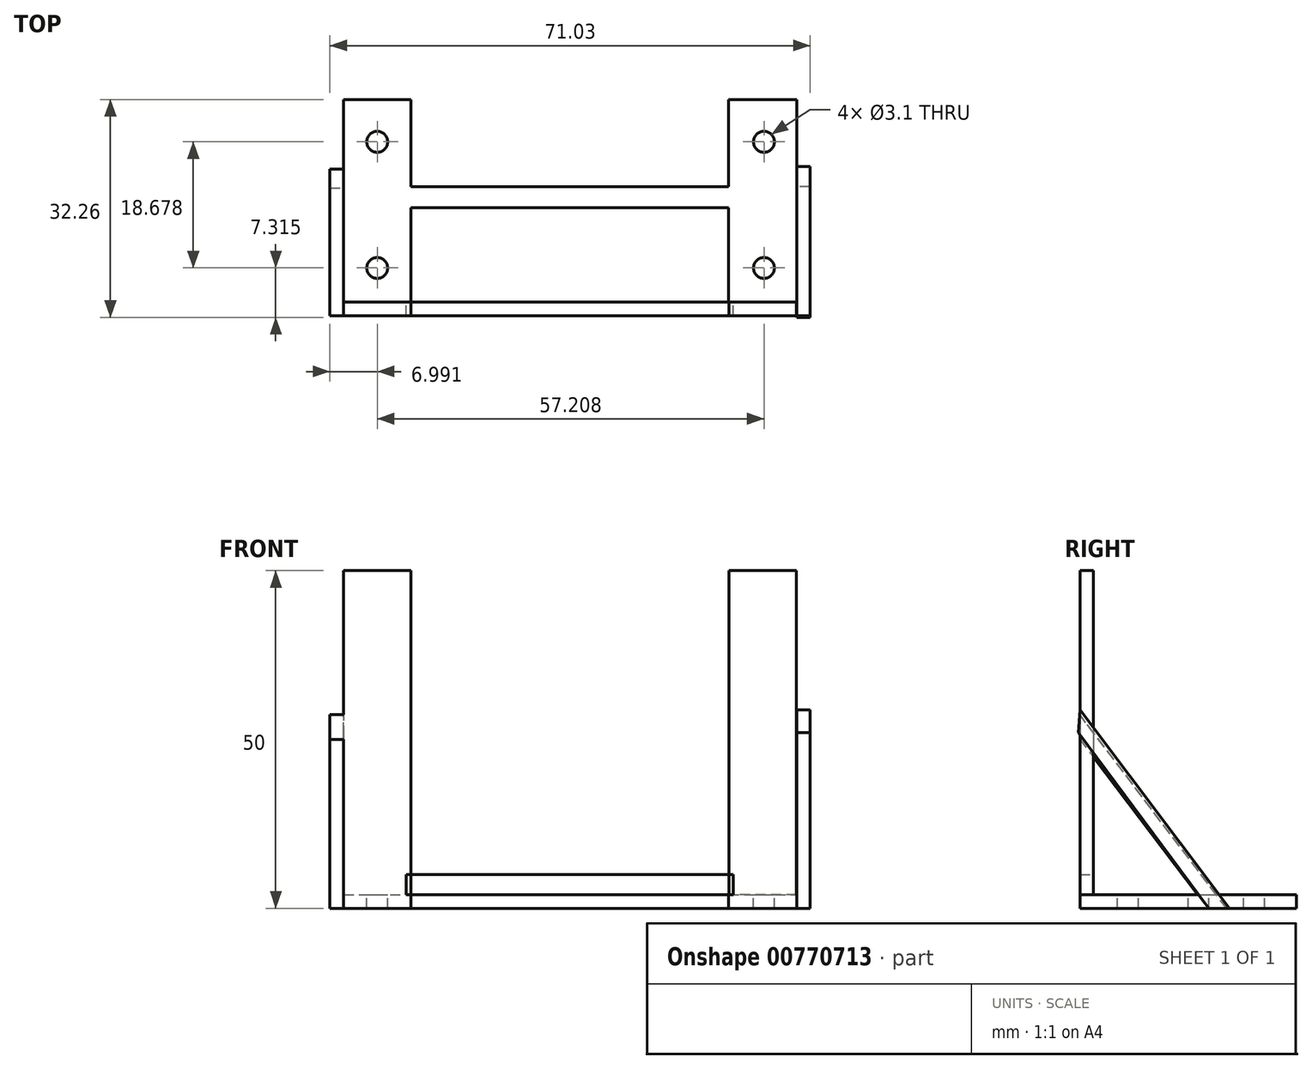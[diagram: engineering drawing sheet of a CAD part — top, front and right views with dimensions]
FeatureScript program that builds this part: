
annotation { "Feature Type Name" : "Feature", "Feature Type Description" : "" }
export const myFeature = defineFeature(function(context is Context, id is Id, definition is map)
    precondition{}
    {
        {
            var Q0;
            Q0=qCreatedBy(makeId("Front.planeOp"),FACE);
            var sketch = newSketch(context, id + "F0", { "sketchPlane" : qUnion([Q0])});
            skLineSegment(sketch, "E0.bottom", {"start": v(-33.5, 24) * mm, "end": v(33.5, 24) * mm});
            skLineSegment(sketch, "E0.top", {"start": v(-33.5, -24) * mm, "end": v(33.5, -24) * mm});
            skLineSegment(sketch, "E0.left", {"start": v(-33.5, 24) * mm, "end": v(-33.5, -24) * mm});
            skLineSegment(sketch, "E0.right", {"start": v(33.5, 24) * mm, "end": v(33.5, -24) * mm});
            skPoint(sketch, "E0.middle", {"position": v(0, 0) * mm});
            skLineSegment(sketch, "E1.bottom", {"start": v(-33.5, 24) * mm, "end": v(-23.5, 24) * mm});
            skLineSegment(sketch, "E1.top", {"start": v(-33.5, -24) * mm, "end": v(-23.5, -24) * mm});
            skLineSegment(sketch, "E1.right", {"start": v(-23.5, 24) * mm, "end": v(-23.5, -24) * mm});
            skLineSegment(sketch, "E2.bottom", {"start": v(33.5, 24) * mm, "end": v(23.5, 24) * mm});
            skLineSegment(sketch, "E2.top", {"start": v(33.5, -24) * mm, "end": v(23.5, -24) * mm});
            skLineSegment(sketch, "E2.right", {"start": v(23.5, 24) * mm, "end": v(23.5, -24) * mm});
            skLineSegment(sketch, "E3.bottom", {"start": v(-23.5, 24) * mm, "end": v(23.5, 24) * mm});
            skLineSegment(sketch, "E3.top", {"start": v(-23.5, 20.9) * mm, "end": v(23.5, 20.9) * mm});
            skLineSegment(sketch, "E3.left", {"start": v(-23.5, 24) * mm, "end": v(-23.5, 20.9) * mm});
            skLineSegment(sketch, "E3.right", {"start": v(23.5, 24) * mm, "end": v(23.5, 20.9) * mm});
            skLineSegment(sketch, "E4.bottom", {"start": v(-23.5, -24) * mm, "end": v(23.5, -24) * mm});
            skLineSegment(sketch, "E4.top", {"start": v(-23.5, -21) * mm, "end": v(23.5, -21) * mm});
            skLineSegment(sketch, "E4.left", {"start": v(-23.5, -24) * mm, "end": v(-23.5, -21) * mm});
            skLineSegment(sketch, "E4.right", {"start": v(23.5, -24) * mm, "end": v(23.5, -21) * mm});
            skSolve(sketch);
        }
        {
            var Q0;
            {var subQ5=sQuery(id+"F0.wireOp",EDGE,"E0.left");Q0=makeQuery(id+"F0.imprint","IMPRINT",FACE,{"disambiguationData":[TD([[makeQuery(id+"F0.imprint","IMPRINT",EDGE,{"derivedFrom":subQ5}),1.0]])]});}
            var Q1;
            {var subQ3=sQuery(id+"F0.wireOp",EDGE,"E0.right");Q1=makeQuery(id+"F0.imprint","IMPRINT",FACE,{"disambiguationData":[TD([[makeQuery(id+"F0.imprint","IMPRINT",EDGE,{"derivedFrom":subQ3}),-1.0]])]});}
            extrude(context, id + "F1", {"entities" : qUnion([Q0, Q1]), "depth" : 2 * mm, "offsetDistance" : 25 * mm});
        }
        {
            var Q0;
            Q0=qCreatedBy(makeId("Front.planeOp"),FACE);
            var sketch = newSketch(context, id + "F2", { "sketchPlane" : qUnion([Q0])});
            skLineSegment(sketch, "E5.left", {"start": v(-23.83, 23.94) * mm, "end": v(-23.83, 20.94) * mm});
            skLineSegment(sketch, "E5.right", {"start": v(23.87, 23.94) * mm, "end": v(23.87, 20.94) * mm});
            skLineSegment(sketch, "E6.bottom", {"start": v(-24.24, -23.98) * mm, "end": v(24.19, -23.98) * mm});
            skLineSegment(sketch, "E6.top", {"start": v(-24.24, -20.98) * mm, "end": v(24.19, -20.98) * mm});
            skLineSegment(sketch, "E6.left", {"start": v(-24.24, -23.98) * mm, "end": v(-24.24, -20.98) * mm});
            skLineSegment(sketch, "E6.right", {"start": v(24.19, -23.98) * mm, "end": v(24.19, -20.98) * mm});
            skSolve(sketch);
        }
        {
            var Q0;
            Q0=makeQuery(id+"F2.imprint","IMPRINT",FACE,{"disambiguationData":[TD([[makeQuery(id+"F2.imprint","IMPRINT",EDGE,{"derivedFrom":sQuery(id+"F2.wireOp",EDGE,"E6.bottom")}),1.0]])]});
            var Q1;
            Q1=makeQuery(id+"F2.imprint","IMPRINT",FACE,{"disambiguationData":[TD([[makeQuery(id+"F2.imprint","IMPRINT",EDGE,{"derivedFrom":sQuery(id+"F2.wireOp",EDGE,"E5.bottom")}),-1.0]])]});
            extrude(context, id + "F3", {"entities" : qUnion([Q0, Q1]), "depth" : 2 * mm, "offsetDistance" : 25 * mm});
        }
        {
            var Q0;
            {var subQ0=sQuery(id+"F0.wireOp",EDGE,"E0.top");Q0=makeQuery(id+"F1.opExtrude","SWEPT_FACE",FACE,{"disambiguationData":[OSD([subQ0]),TDD([makeQuery(id+"F0.imprint","IMPRINT",EDGE,{"disambiguationData":[TD([[makeQuery(id+"F0.imprint","INTERSECT",VERTEX,{"derivedFrom":[subQ0,sQuery(id+"F0.wireOp",EDGE,"E1.right")]}),1.0]])],"derivedFrom":subQ0})])]});}
            var sketch = newSketch(context, id + "F4", { "sketchPlane" : qUnion([Q0])});
            skLineSegment(sketch, "E7.bottom", {"start": v(-33.5, 2) * mm, "end": v(-23.55, 2) * mm});
            skLineSegment(sketch, "E7.top", {"start": v(-33.5, -30.02) * mm, "end": v(-23.55, -30.02) * mm});
            skLineSegment(sketch, "E7.left", {"start": v(-33.5, 2) * mm, "end": v(-33.5, -30.02) * mm});
            skLineSegment(sketch, "E7.right", {"start": v(-23.55, 2) * mm, "end": v(-23.55, -30.02) * mm});
            skLineSegment(sketch, "E8.bottom", {"start": v(33.53, 2) * mm, "end": v(23.47, 2) * mm});
            skLineSegment(sketch, "E8.top", {"start": v(33.53, -30.02) * mm, "end": v(23.47, -30.02) * mm});
            skLineSegment(sketch, "E8.left", {"start": v(33.53, 2) * mm, "end": v(33.53, -30.02) * mm});
            skLineSegment(sketch, "E8.right", {"start": v(23.47, 2) * mm, "end": v(23.47, -30.02) * mm});
            skLineSegment(sketch, "E9.bottom", {"start": v(-23.5, 2) * mm, "end": v(23.47, 2) * mm});
            skLineSegment(sketch, "E9.top", {"start": v(-23.5, -2.98) * mm, "end": v(23.47, -2.98) * mm});
            skLineSegment(sketch, "E9.left", {"start": v(-23.5, 2) * mm, "end": v(-23.5, -2.98) * mm});
            skLineSegment(sketch, "E9.right", {"start": v(23.47, 2) * mm, "end": v(23.47, -2.98) * mm});
            skLineSegment(sketch, "E10.bottom", {"start": v(-23.55, -14.01) * mm, "end": v(23.47, -14.01) * mm});
            skLineSegment(sketch, "E10.top", {"start": v(-23.55, -17.1) * mm, "end": v(23.47, -17.1) * mm});
            skLineSegment(sketch, "E10.left", {"start": v(-23.55, -14.01) * mm, "end": v(-23.55, -17.1) * mm});
            skLineSegment(sketch, "E10.right", {"start": v(23.47, -14.01) * mm, "end": v(23.47, -17.1) * mm});
            skCircle(sketch, "E11", {"center": v(-28.5, -5.07) * mm, "radius": 1.55 * mm});
            skCircle(sketch, "E12", {"center": v(-28.5, -23.75) * mm, "radius": 1.55 * mm});
            skCircle(sketch, "E13", {"center": v(28.7, -23.75) * mm, "radius": 1.55 * mm});
            skCircle(sketch, "E14", {"center": v(28.7, -5.07) * mm, "radius": 1.55 * mm});
            skSolve(sketch);
        }
        {
            var Q0;
            {var subQ6=sQuery(id+"F4.wireOp",EDGE,"E7.top");Q0=makeQuery(id+"F4.imprint","IMPRINT",FACE,{"disambiguationData":[TD([[makeQuery(id+"F4.imprint","IMPRINT",EDGE,{"derivedFrom":subQ6}),1.0]])]});}
            var Q1;
            {var subQ0=sQuery(id+"F4.wireOp",EDGE,"E7.bottom");Q1=makeQuery(id+"F4.imprint","IMPRINT",FACE,{"disambiguationData":[TD([[makeQuery(id+"F4.imprint","IMPRINT",EDGE,{"derivedFrom":subQ0}),-1.0]])]});}
            var Q2;
            Q2=makeQuery(id+"F4.imprint","IMPRINT",FACE,{"disambiguationData":[TD([[makeQuery(id+"F4.imprint","IMPRINT",EDGE,{"derivedFrom":sQuery(id+"F4.wireOp",EDGE,"E8.bottom")}),1.0]])]});
            var Q3;
            Q3=makeQuery(id+"F4.imprint","IMPRINT",FACE,{"disambiguationData":[TD([[makeQuery(id+"F4.imprint","IMPRINT",EDGE,{"derivedFrom":sQuery(id+"F4.wireOp",EDGE,"E10.bottom")}),-1.0]])]});
            extrude(context, id + "F5", {"entities" : qUnion([Q0, Q1, Q2, Q3]), "operationType" : NewBodyOperationType.ADD, "depth" : 2 * mm, "offsetDistance" : 25 * mm});
        }
        {
            var Q0;
            Q0=makeQuery(id+"F5.opExtrude","SWEPT_FACE",FACE,{"disambiguationData":[OSD([sQuery(id+"F4.wireOp",EDGE,"E8.left")])]});
            var sketch = newSketch(context, id + "F6", { "sketchPlane" : qUnion([Q0])});
            skLineSegment(sketch, "E15", {"start": v(-2.24, 0) * mm, "end": v(17.1, -26) * mm});
            skLineSegment(sketch, "E16", {"start": v(17.1, -26) * mm, "end": v(20.1, -26) * mm});
            skLineSegment(sketch, "E17", {"start": v(20.1, -26) * mm, "end": v(-2, 3.36) * mm});
            skLineSegment(sketch, "E18", {"start": v(-2, 3.36) * mm, "end": v(-2.24, 0) * mm});
            skSolve(sketch);
        }
        {
            var Q0;
            {var subQ0=sQuery(id+"F6.wireOp",EDGE,"E18");Q0=makeQuery(id+"F6.imprint","IMPRINT",FACE,{"disambiguationData":[TD([[makeQuery(id+"F6.imprint","IMPRINT",EDGE,{"derivedFrom":subQ0}),1.0]])]});}
            var Q1;
            {var subQ0=sQuery(id+"F6.wireOp",EDGE,"E16");Q1=makeQuery(id+"F6.imprint","IMPRINT",FACE,{"disambiguationData":[TD([[makeQuery(id+"F6.imprint","IMPRINT",EDGE,{"derivedFrom":subQ0}),1.0]])]});}
            extrude(context, id + "F7", {"entities" : qUnion([Q0, Q1]), "operationType" : NewBodyOperationType.ADD, "depth" : 2 * mm, "offsetDistance" : 25 * mm});
        }
        {
            var Q0;
            Q0=makeQuery(id+"F5.boolean.opBoolean","MERGE",FACE,{"derivedFrom":[makeQuery(id+"F1.opExtrude","SWEPT_FACE",FACE,{"disambiguationData":[OSD([sQuery(id+"F0.wireOp",EDGE,"E0.left")])]}),makeQuery(id+"F5.opExtrude","SWEPT_FACE",FACE,{"disambiguationData":[OSD([sQuery(id+"F4.wireOp",EDGE,"E7.left")])]})]});
            var sketch = newSketch(context, id + "F8", { "sketchPlane" : qUnion([Q0])});
            skLineSegment(sketch, "E19", {"start": v(-19.7, -26) * mm, "end": v(2, 2.65) * mm});
            skLineSegment(sketch, "E20", {"start": v(2, 2.65) * mm, "end": v(2, -1) * mm});
            skLineSegment(sketch, "E21", {"start": v(2, -1) * mm, "end": v(-16.94, -26) * mm});
            skLineSegment(sketch, "E22", {"start": v(-16.94, -26) * mm, "end": v(-19.7, -26) * mm});
            skSolve(sketch);
        }
        {
            var Q0;
            {var subQ0=sQuery(id+"F8.wireOp",EDGE,"E20");Q0=makeQuery(id+"F8.imprint","IMPRINT",FACE,{"disambiguationData":[TD([[makeQuery(id+"F8.imprint","IMPRINT",EDGE,{"derivedFrom":subQ0}),-1.0]])]});}
            var Q1;
            {var subQ0=sQuery(id+"F8.wireOp",EDGE,"E19");var subQ1=makeQuery(id+"F5.opExtrude","CAP_EDGE",EDGE,{"disambiguationData":[OSD([sQuery(id+"F4.wireOp",EDGE,"E7.left")])],"isStart":true});var subQ2=makeQuery(id+"F8.imprint","INTERSECT",VERTEX,{"derivedFrom":[subQ1,subQ0]});Q1=makeQuery(id+"F8.imprint","IMPRINT",FACE,{"disambiguationData":[TD([[makeQuery(id+"F8.imprint","IMPRINT",EDGE,{"disambiguationData":[TD([[subQ2,-1.0]])],"derivedFrom":subQ0}),-1.0]])]});}
            var Q2;
            {var subQ0=sQuery(id+"F8.wireOp",EDGE,"E22");Q2=makeQuery(id+"F8.imprint","IMPRINT",FACE,{"disambiguationData":[TD([[makeQuery(id+"F8.imprint","IMPRINT",EDGE,{"derivedFrom":subQ0}),-1.0]])]});}
            extrude(context, id + "F9", {"entities" : qUnion([Q0, Q1, Q2]), "operationType" : NewBodyOperationType.ADD, "depth" : 2 * mm, "offsetDistance" : 25 * mm});
        }
    });
